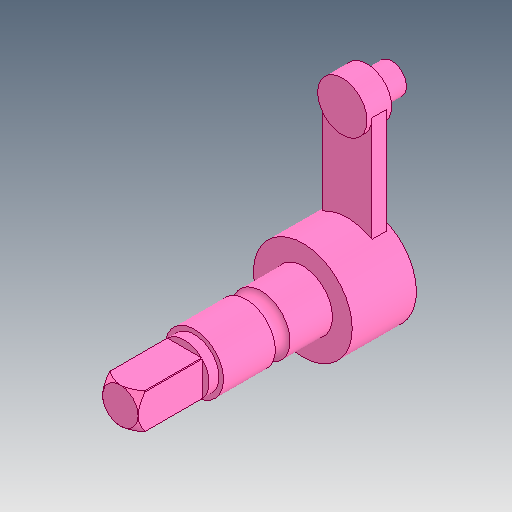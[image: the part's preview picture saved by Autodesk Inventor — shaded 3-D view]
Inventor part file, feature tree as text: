
AUTODESK INVENTOR PART (.ipt)
format: ipt  version: 2017 (Build 210142000, 142)  size: 200,704 bytes
history: native  units: mm
features: sketch x9, extrude x8, other x2, mirror x1, chamfer x1, revolve x1, projected_geometry x1
ambient origin geometry x8: Origin, YZ Plane, XZ Plane, XY Plane, X Axis, Y Axis, Z Axis, Center Point
bodies: Solid1 (feature_tree)
feature tree (23):
  extrude  "Extrusion1"  Depth=6.0mm
  extrude  "Extrusion2"  Depth=12.0mm
  mirror  "Mirror1"
  extrude  "Extrusion3"  Depth=5.0mm TaperAngle=0.0deg
  extrude  "Extrusion4"  Depth=3.0mm TaperAngle=0.0deg
  extrude  "Extrusion5"  Depth=35.0mm TaperAngle=0.0deg
  extrude  "Extrusion6"  Depth=5.0mm TaperAngle=0.0deg
  chamfer  "Chamfer1"  Distance=15.0mm
  extrude  "Extrusion7"  Depth=13.0mm TaperAngle=0.0deg
  other  "Work Point1"
  sketch  "Sketch8"  dims[d18=10.0mm d19=15.0mm d20=0.0mm]
  revolve  "Revolution1"  [1 undecoded]
  extrude  "Extrusion8"  TaperAngle=90.0deg  [1 undecoded]
  sketch  "Sketch1"  dims[d0=30.0mm d1=6.0mm]
  sketch  "Sketch2"  dims[d2=10.0mm d3=12.0mm]
  sketch  "Sketch3"  dims[d4=20.0mm d6=5.0mm d7=0.0mm]
  sketch  "Sketch4"  dims[d8=1.0mm d9=0.0mm d10=3.0mm d11=0.0mm]
  sketch  "Sketch5"  dims[d12=0.1mm d13=35.0mm d14=0.0mm]
  sketch  "Sketch6"  dims[d15=6.0mm d16=5.0mm d17=0.0mm]
  other  "Work Axis1"
  sketch  "Sketch9"  dims[d21=1.4mm d22=2.0mm d23=45.0deg d24=13.0mm d25=0.0mm]
  sketch  "Sketch10"  dims[d26=3.0mm d27=12.0mm d28=90.0deg d29=5.0mm d30=0.0mm]
  projected_geometry  "Projected Loop1"
note: 2 required parameter values undecoded (feature->parameter linkage not recoverable at this tier; creation-order binding heuristic only, values carry confidence <= 0.55)